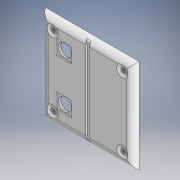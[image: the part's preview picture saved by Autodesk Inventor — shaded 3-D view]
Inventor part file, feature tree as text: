
AUTODESK INVENTOR PART (.ipt)
format: ipt  version: 2018 (Build 220112000, 112)  size: 359,424 bytes
history: native  units: in
note: dims shown in document units (in); Inventor stores cm internally (conversion verified against a paired STEP export)
features: extrude x14, sketch x14, fillet x5, chamfer x1
ambient origin geometry x8: Origin, YZ Plane, XZ Plane, XY Plane, X Axis, Y Axis, Z Axis, Center Point
bodies: Solid1 (feature_tree)
feature tree (34):
  extrude  "Extrusion1"  Depth=4.5in
  extrude  "Extrusion2"  Depth=0.1575in
  extrude  "Extrusion3"  Depth=1.125in
  fillet  "Fillet1"  Radius=1.125in
  sketch  "Sketch4"  dims[d8=0.25in d9=0.0in d10=0.0984in d11=0.0984in]
  sketch  "Sketch5"  dims[d12=0.0787in d13=0.0in d14=0.3937in]
  extrude  "Extrusion6"  Depth=0.0984in
  fillet  "Fillet4"  Radius=0.0984in
  extrude  "Extrusion7"  Depth=0.3937in
  extrude  "Extrusion8"  Depth=4.0in
  extrude  "Extrusion9"  Depth=0.0394in TaperAngle=0.0deg
  fillet  "Fillet6"  Radius=0.4724in
  fillet  "Fillet7"  Radius=0.0625in
  extrude  "Extrusion10"  Depth=0.25in TaperAngle=0.0deg
  extrude  "Extrusion11"  Depth=3.375in
  extrude  "Extrusion12"  Depth=0.1772in
  fillet  "Fillet8"  Radius=0.1772in
  extrude  "Extrusion13"  Depth=0.25in TaperAngle=0.0deg
  extrude  "Extrusion14"  Depth=0.3051in
  chamfer  "Chamfer1"  Distance=0.0591in
  extrude  "Extrusion15"  Depth=0.1969in
  extrude  "Extrusion16"  Depth=0.1969in
  sketch  "Sketch1"  dims[d0=4.5in d1=4.5in]
  sketch  "Sketch2"  dims[d2=0.1575in d3=0.0in d4=0.6299in]
  sketch  "Sketch3"  dims[d5=0.6299in d6=1.125in d7=1.125in]
  sketch  "Sketch6"  dims[d23=4.0in d24=4.0in]
  sketch  "Sketch7"  dims[d29=0.125in d30=0.0394in d31=0.0in d34=0.4724in d35=0.0625in]
  sketch  "Sketch8"  dims[d36=0.0625in d37=0.25in d38=0.0in]
  sketch  "Sketch9"  dims[d43=3.375in d44=3.375in]
  sketch  "Sketch10"  dims[d45=0.1772in d46=0.1772in d47=0.1772in]
  sketch  "Sketch11"  dims[d48=0.1772in d49=0.25in d50=0.0in]
  sketch  "Sketch12"  dims[d52=0.3051in d53=0.3051in]
  sketch  "Sketch13"  dims[d54=0.3051in]
  sketch  "Sketch14"  dims[d55=0.3051in d56=0.0591in d57=0.0in d58=0.1969in d59=0.1969in d60=0.0689in d61=0.9646in d62=0.0689in d63=0.4823in d64=0.4823in d65=1.3583in d66=0.6791in d67=0.6791in d68=0.0689in d69=0.0689in d70=1.4567in d71=0.1969in d72=0.1969in d73=0.1969in d74=0.1969in d75=0.0787in d76=0.0in d77=0.1575in d78=0.3937in d79=0.5906in d80=0.0in d81=0.4626in d82=0.7874in d83=0.0in d84=0.1181in d85=0.1969in d86=0.7283in d87=0.7283in d88=0.7283in d89=0.7283in d90=0.0394in d91=0.0in d92=1.0433in d94=0.1181in d95=0.0in d97=0.0in d98=0.1083in d99=0.0394in d100=0.125in d101=45.0deg d102=0.315in d103=0.0in d104=1.0in d105=0.5906in d106=0.5906in d107=0.0787in d108=0.0in]
